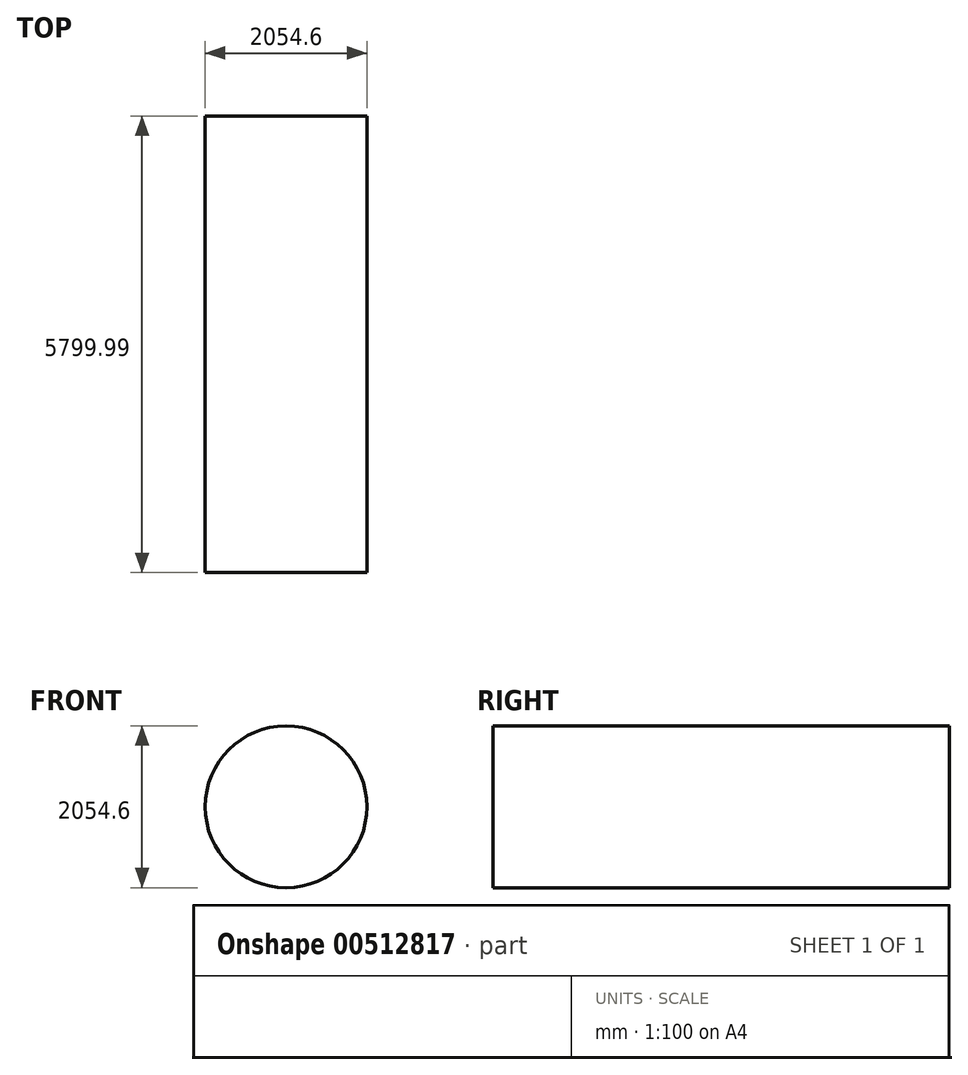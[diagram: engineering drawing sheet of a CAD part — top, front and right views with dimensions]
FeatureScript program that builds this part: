
annotation { "Feature Type Name" : "Feature", "Feature Type Description" : "" }
export const myFeature = defineFeature(function(context is Context, id is Id, definition is map)
    precondition{}
    {
        {
            var Q0;
            Q0=qCreatedBy(makeId("Front.planeOp"),FACE);
            var sketch = newSketch(context, id + "F0", { "sketchPlane" : qUnion([Q0])});
            skCircle(sketch, "E0", {"center": v(-11.4, 20.76) * mm, "radius": 1027.3 * mm});
            skSolve(sketch);
        }
        {
            var Q0;
            Q0=sQuery(id+"F0.wireOp",EDGE,"E0");
            extrude(context, id + "F1", {"bodyType" : ToolBodyType.SURFACE, "surfaceEntities" : qUnion([Q0]), "depth" : 5799.99 * mm});
        }
    });
